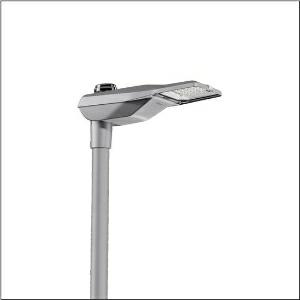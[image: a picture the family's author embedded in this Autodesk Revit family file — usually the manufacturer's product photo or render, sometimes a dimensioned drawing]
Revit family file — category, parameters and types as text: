
# Revit family: streetlight_sl_21_micro___st0_8a_5xe5c47n08db_8458
name_source: partatom
category: Lighting Fixtures
units: mm (PartAtom-declared; Revit-internal decimal feet)

## family parameters
Cut with Voids When Loaded = No
Host = Face
Light Source = No
Part Type = Normal
Room Calculation Point = No
Round Connector Dimension = Use Diameter
Shared = No

## types (1)
- --- (1 x LED, 5320 lm, 39.1 W, 4000K)
    Apparent Load = 39 VA
    CIE Flux Codes = 38 75 97 100 100
    Color Rendering = 70
    Color Temperature = 4000K
    Default Elevation = 1800 mm
    Description = Streetlight SL 21 micro, mast luminaire, primary light control with lens, of PMMA, primary optical cover: cover, of toughened safety glass, transparent, light distribution: ST0.8a, light emission: direct distribution, primary light characteristic: asymmetric, installation type: post-top, LED, 3G 1.5mm², High Power LED, rated luminous flux: 5.320lm, luminous efficacy: 136lm/W, light colour: 740, colour temperature: 4000K, control gear: NEMA (7pin), control: overheat protection, pre-setting: linear dimming characteristic, constant luminous flux control, time-dependent luminous flux control, flexible luminous flux parameterisation, mains connection: 230..240V, AC, 50/60Hz, connection cable pre-assembled, cable length: 6,5m, wiring characteristics: H07RN-F, start of lifetime: 39W, end of service life: 41W, reduction: 18W, luminaire housing, of diecast aluminium (EN AC-44300), powder-coated, SITECO metallic grey (DB 702S), corrosivity category C5 high according to DIN EN ISO 12944, multi-level sealing system, sealing non-destructively replaceable, inclination adjustable: 0°, 5°, 10°, 15°, length: 528mm, width: 235mm, height: 110mm, spigot size: 76/60mm (post-top), mounting height: 4..8m, protection rating (complete): IP66, insulation class (complete): insulation class I (protective earthing), certification: CE, ENEC, ENEC+, VDE, impact resistance: IK10, permissible operating ambient temperature for outdoor applications: -40..+50°C, standard-compliant lighting for roads and squares, packaging unit: 1 piece

Light Distribution: ST0.8a
    Height = 110 mm
    Lamp = 1 x LED
    Lamp Light Flux = 5320 lm
    Lamp Power = 39.1 W
    Lamp count = 1
    Length = 528 mm
    Luminous efficacy = 136 lm/W
    Manufacturer = Siteco
    ModVariant = No
    Model = 5XE5C47N08DB
    Number of Poles = 1
    OnlyDefault = Yes
    Power Factor = 1
    Product Name = Streetlight SL 21 micro | ST0.8a
    Product group = mast luminaire | pylon top
    ProductGroupID = 6100
    Protection Class = Protection class I
    Protection Degree = IP 66
    RLX_Detail_Level = 1
    RLX_Emergency_Light_Flux = 0 lm
    RLX_Emergency_Type = 0
    RLX_Emergency_Type_DB = No
    RlxData = <blob elided: 99217 chars, md5=18d84b20>
    Socket = socket
    Standby Power = 0 W
    System Light Flux = 5320 lm
    System Power = 39 W
    Type Comments = factory setting: luminous flux: 100 % | dim-lin: 254 | 765 mA
    Type Image = l_1294375.jpg
    URL = http://relux.com
    VarID = @adj_133799
    Voltage = 0 V
    Weight = 0.00 kg
    Width = 235 mm

## geometry (parser evidence)
native form markers: Blend x4, Sweep x10
no freeform markers — native parametric forms only
